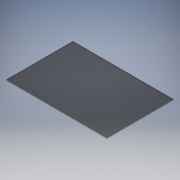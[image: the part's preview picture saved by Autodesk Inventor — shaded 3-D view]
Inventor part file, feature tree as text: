
AUTODESK INVENTOR PART (.ipt)
format: ipt  version: 2016 (Build 200138000, 138)  size: 101,376 bytes
history: native  units: mm
features: extrude x1, sketch x1
ambient origin geometry x8: Origin, YZ Plane, XZ Plane, XY Plane, X Axis, Y Axis, Z Axis, Center Point
bodies: 实体1 (feature_tree)
feature tree (2):
  extrude  "拉伸1"  Depth=500.0mm
  sketch  "草图1"  dims[d0=755.0mm d1=500.0mm d2=5.0mm d3=0.0mm]
